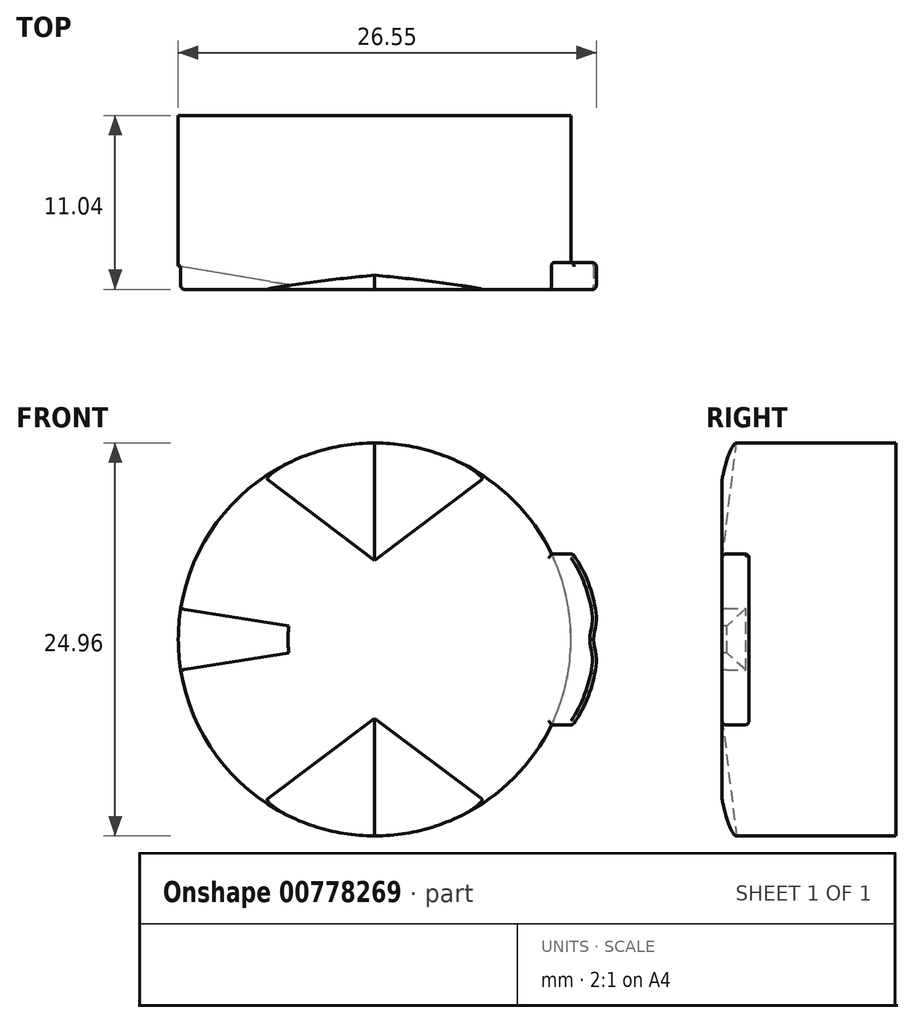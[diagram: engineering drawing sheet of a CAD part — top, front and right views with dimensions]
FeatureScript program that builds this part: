
annotation { "Feature Type Name" : "Feature", "Feature Type Description" : "" }
export const myFeature = defineFeature(function(context is Context, id is Id, definition is map)
    precondition{}
    {
        {
            var Q0;
            Q0=qCreatedBy(makeId("Front.planeOp"),FACE);
            var sketch = newSketch(context, id + "F0", { "sketchPlane" : qUnion([Q0])});
            skCircle(sketch, "E0", {"center": v(0, 0) * mm, "radius": 12.47 * mm});
            skSolve(sketch);
        }
        {
            var Q0;
            Q0=makeQuery(id+"F0.imprint","IMPRINT",FACE,{"disambiguationData":[TD([[makeQuery(id+"F0.imprint","IMPRINT",EDGE,{"derivedFrom":sQuery(id+"F0.wireOp",EDGE,"E0")}),1.0]])]});
            extrude(context, id + "F1", {"entities" : qUnion([Q0]), "depth" : 3.04 * mm, "offsetDistance" : 25 * mm});
        }
        {
            var Q0;
            Q0=makeQuery(id+"F1.opExtrude","CAP_FACE",FACE,{"disambiguationData":[OSD([sQuery(id+"F0.wireOp",EDGE,"E0")])],"isStart":false});
            var sketch = newSketch(context, id + "F2", { "sketchPlane" : qUnion([Q0])});
            skLineSegment(sketch, "E1", {"start": v(0, 0) * mm, "end": v(-7.03, 10.3) * mm, "construction": true});
            skLineSegment(sketch, "E2", {"start": v(0, 0) * mm, "end": v(0, 12.47) * mm, "construction": true});
            skLineSegment(sketch, "E3.MirrorCS", {"start": v(0, 0) * mm, "end": v(7.03, 10.3) * mm, "construction": true});
            skLineSegment(sketch, "E4", {"start": v(0, 0) * mm, "end": v(12.47, 0) * mm, "construction": true});
            skLineSegment(sketch, "E5.MirrorCS", {"start": v(0, 0) * mm, "end": v(7.03, -10.3) * mm, "construction": true});
            skLineSegment(sketch, "E6.MirrorCS", {"start": v(0, 0) * mm, "end": v(-7.03, -10.3) * mm, "construction": true});
            skLineSegment(sketch, "E7", {"start": v(11.42, -5.02) * mm, "end": v(-11.42, -5.02) * mm, "construction": true});
            skLineSegment(sketch, "E8", {"start": v(0, -5.02) * mm, "end": v(0, -12.47) * mm, "construction": true});
            skLineSegment(sketch, "E9", {"start": v(-7.03, -10.3) * mm, "end": v(0, -5.02) * mm});
            skLineSegment(sketch, "E10", {"start": v(7.03, -10.3) * mm, "end": v(0, -5.02) * mm, "construction": true});
            skLineSegment(sketch, "E11.MirrorCS", {"start": v(7.03, 10.3) * mm, "end": v(0, 5.02) * mm, "construction": true});
            skLineSegment(sketch, "E12.MirrorCS", {"start": v(-7.03, 10.3) * mm, "end": v(0, 5.02) * mm, "construction": true});
            skLineSegment(sketch, "E13", {"start": v(0, -5.02) * mm, "end": v(0, -12.47) * mm});
            skArc(sketch, "E14", {"start": v(0, -12.47) * mm, "mid": v(-3.68, -11.92) * mm, "end": v(-7.03, -10.3) * mm});
            skSolve(sketch);
        }
        {
            var Q0;
            Q0=qCreatedBy(makeId("Right.planeOp"),FACE);
            var sketch = newSketch(context, id + "F3", { "sketchPlane" : qUnion([Q0])});
            skLineSegment(sketch, "E15.0", {"start": v(-3.04, -5.02) * mm, "end": v(-3.04, -12.47) * mm});
            skLineSegment(sketch, "E16", {"start": v(-3.04, -12.47) * mm, "end": v(-2.14, -12.47) * mm});
            skLineSegment(sketch, "E17", {"start": v(-2.14, -12.47) * mm, "end": v(-3.04, -5.02) * mm});
            skLineSegment(sketch, "E18", {"start": v(-3.04, -5.02) * mm, "end": v(-7.03, -5.02) * mm, "construction": true});
            skPoint(sketch, "E19.0", {"position": v(-3.04, 0) * mm});
            skLineSegment(sketch, "E20", {"start": v(-3.04, 0) * mm, "end": v(-13.95, 0) * mm});
            skLineSegment(sketch, "E21.MirrorCS", {"start": v(-3.04, 12.47) * mm, "end": v(-2.14, 12.47) * mm});
            skLineSegment(sketch, "E22.0", {"start": v(-3.04, 0) * mm, "end": v(-3.04, 12.47) * mm});
            skPoint(sketch, "E23.0", {"position": v(-3.04, 7.66) * mm});
            skLineSegment(sketch, "E24.0", {"start": v(-3.04, 10.3) * mm, "end": v(-3.04, 5.02) * mm});
            skLineSegment(sketch, "E25", {"start": v(-3.04, 5.02) * mm, "end": v(-2.14, 12.47) * mm});
            skLineSegment(sketch, "E26", {"start": v(-3.04, 10.3) * mm, "end": v(-2.4, 10.3) * mm});
            skSolve(sketch);
        }
        {
            var Q0;
            Q0=sQuery(id+"F2.wireOp",EDGE,"E7");
            cPoint(context, id + "F4", {"entities" : qUnion([Q0]), "parameter" : 0.5});
        }
        {
            var Q0;
            Q0=qCreatedBy(id+"F4",VERTEX);
            var Q1;
            Q1=sQuery(id+"F2.wireOp",VERTEX,"E6.MirrorCS.end");
            var Q2;
            Q2=sQuery(id+"F3.wireOp",VERTEX,"E16.end");
            cPlane(context, id + "F5", {"entities" : qUnion([Q0, Q1, Q2]), "cplaneType" : CPlaneType.THREE_POINT, "offset" : 25 * mm, "width" : 150 * mm, "height" : 150 * mm});
        }
        {
            var Q0;
            Q0=qSketchRegion(id+"F2",true);
            var Q1;
            Q1=qCreatedBy(id+"F5.planeOp",FACE);
            extrude(context, id + "F6", {"entities" : qUnion([Q0]), "operationType" : NewBodyOperationType.REMOVE, "endBound" : BoundingType.UP_TO_SURFACE, "oppositeDirection" : true, "depth" : 25 * mm, "endBoundEntityFace" : qUnion([Q1]), "offsetDistance" : 25 * mm});
        }
        {
            var Q0;
            Q0=sQuery(id+"F2.wireOp",VERTEX,"E8.start");
            var Q1;
            Q1=makeQuery(id+"F6.boolean.opBoolean","COPY",VERTEX,{"derivedFrom":makeQuery(id+"F6.opExtrude","CAP_VERTEX",VERTEX,{"disambiguationData":[OSD([sQuery(id+"F2.wireOp",EDGE,"E13"),sQuery(id+"F2.wireOp",EDGE,"E14")])],"isStart":false})});
            var Q2;
            Q2=sQuery(id+"F2.wireOp",VERTEX,"E5.MirrorCS.end");
            cPlane(context, id + "F7", {"entities" : qUnion([Q0, Q1, Q2]), "cplaneType" : CPlaneType.THREE_POINT, "offset" : 25 * mm, "width" : 150 * mm, "height" : 150 * mm});
        }
        {
            var Q0;
            {var subQ0=sQuery(id+"F2.wireOp",EDGE,"E9");Q0=makeQuery(id+"F2.imprint","IMPRINT",FACE,{"disambiguationData":[TD([[makeQuery(id+"F2.imprint","IMPRINT",EDGE,{"derivedFrom":subQ0}),1.0]])]});}
            var sketch = newSketch(context, id + "F8", { "sketchPlane" : qUnion([Q0])});
            skLineSegment(sketch, "E27.0", {"start": v(7.03, -10.3) * mm, "end": v(0, -5.02) * mm});
            skLineSegment(sketch, "E28.0", {"start": v(0, -5.02) * mm, "end": v(0, -12.47) * mm});
            skArc(sketch, "E29", {"start": v(7.03, -10.3) * mm, "mid": v(3.68, -11.92) * mm, "end": v(0, -12.48) * mm});
            skSolve(sketch);
        }
        {
            var Q0;
            Q0=qSketchRegion(id+"F8",true);
            var Q1;
            Q1=qCreatedBy(id+"F7.planeOp",FACE);
            extrude(context, id + "F9", {"entities" : qUnion([Q0]), "operationType" : NewBodyOperationType.REMOVE, "endBound" : BoundingType.UP_TO_SURFACE, "oppositeDirection" : true, "depth" : 25 * mm, "endBoundEntityFace" : qUnion([Q1]), "offsetDistance" : 25 * mm});
        }
        {
            var Q0;
            Q0=sQuery(id+"F3.wireOp",VERTEX,"E26.end");
            var Q1;
            Q1=sQuery(id+"F2.wireOp",VERTEX,"E1.end");
            var Q2;
            Q2=sQuery(id+"F2.wireOp",VERTEX,"E3.MirrorCS.end");
            cPlane(context, id + "F10", {"entities" : qUnion([Q0, Q1, Q2]), "cplaneType" : CPlaneType.THREE_POINT, "offset" : 25 * mm, "width" : 150 * mm, "height" : 150 * mm});
        }
        {
            var Q0;
            Q0=qCreatedBy(id+"F10.planeOp",FACE);
            var sketch = newSketch(context, id + "F11", { "sketchPlane" : qUnion([Q0])});
            skPoint(sketch, "E30.0", {"position": v(7.03, 3.04) * mm});
            skPoint(sketch, "E31.0", {"position": v(0, 2.4) * mm});
            skPoint(sketch, "E32.0", {"position": v(-7.03, 3.04) * mm});
            skLineSegment(sketch, "E33", {"start": v(0, 2.4) * mm, "end": v(7.03, 3.04) * mm});
            skLineSegment(sketch, "E34", {"start": v(-7.03, 3.04) * mm, "end": v(0, 2.4) * mm});
            skLineSegment(sketch, "E35", {"start": v(-7.03, 3.04) * mm, "end": v(7.03, 3.04) * mm});
            skSolve(sketch);
        }
        {
            var Q0;
            Q0=qCreatedBy(makeId("Right.planeOp"),FACE);
            var sketch = newSketch(context, id + "F12", { "sketchPlane" : qUnion([Q0])});
            skPoint(sketch, "E36.0", {"position": v(-2.4, 10.3) * mm});
            skPoint(sketch, "E37.0", {"position": v(-3.04, 5.02) * mm});
            skLineSegment(sketch, "E38", {"start": v(-3.04, 5.02) * mm, "end": v(-2.4, 10.3) * mm});
            skPoint(sketch, "E39.0", {"position": v(-2.14, 12.47) * mm});
            skLineSegment(sketch, "E40", {"start": v(-2.4, 10.3) * mm, "end": v(-2.14, 12.47) * mm});
            skSolve(sketch);
        }
        {
            var Q0;
            Q0=sQuery(id+"F12.wireOp",VERTEX,"E39.0");
            var Q1;
            Q1=sQuery(id+"F12.wireOp",VERTEX,"E37.0");
            var Q2;
            Q2=sQuery(id+"F11.wireOp",VERTEX,"E32.0");
            cPlane(context, id + "F13", {"entities" : qUnion([Q0, Q1, Q2]), "cplaneType" : CPlaneType.THREE_POINT, "offset" : 25 * mm, "width" : 150 * mm, "height" : 150 * mm});
        }
        {
            var Q0;
            Q0=sQuery(id+"F12.wireOp",VERTEX,"E39.0");
            var Q1;
            Q1=sQuery(id+"F12.wireOp",VERTEX,"E37.0");
            var Q2;
            Q2=sQuery(id+"F11.wireOp",VERTEX,"E30.0");
            cPlane(context, id + "F14", {"entities" : qUnion([Q0, Q1, Q2]), "cplaneType" : CPlaneType.THREE_POINT, "offset" : 25 * mm, "width" : 150 * mm, "height" : 150 * mm});
        }
        {
            var Q0;
            {var subQ0=sQuery(id+"F2.wireOp",EDGE,"E9");Q0=makeQuery(id+"F2.imprint","IMPRINT",FACE,{"disambiguationData":[TD([[makeQuery(id+"F2.imprint","IMPRINT",EDGE,{"derivedFrom":subQ0}),1.0]])]});}
            var sketch = newSketch(context, id + "F15", { "sketchPlane" : qUnion([Q0])});
            skLineSegment(sketch, "E41.0", {"start": v(7.03, 10.3) * mm, "end": v(0, 5.02) * mm});
            skPoint(sketch, "E42.0", {"position": v(0, 12.47) * mm});
            skLineSegment(sketch, "E43", {"start": v(0, 5.02) * mm, "end": v(0, 12.47) * mm});
            skArc(sketch, "E44", {"start": v(7.03, 10.3) * mm, "mid": v(3.68, 11.92) * mm, "end": v(0, 12.48) * mm});
            skSolve(sketch);
        }
        {
            var Q0;
            Q0=qSketchRegion(id+"F15",true);
            var Q1;
            Q1=qCreatedBy(id+"F14.planeOp",FACE);
            extrude(context, id + "F16", {"entities" : qUnion([Q0]), "operationType" : NewBodyOperationType.REMOVE, "endBound" : BoundingType.UP_TO_SURFACE, "oppositeDirection" : true, "depth" : 25 * mm, "endBoundEntityFace" : qUnion([Q1]), "offsetDistance" : 25 * mm});
        }
        {
            var Q0;
            {var subQ0=sQuery(id+"F2.wireOp",EDGE,"E9");Q0=makeQuery(id+"F2.imprint","IMPRINT",FACE,{"disambiguationData":[TD([[makeQuery(id+"F2.imprint","IMPRINT",EDGE,{"derivedFrom":subQ0}),1.0]])]});}
            var sketch = newSketch(context, id + "F17", { "sketchPlane" : qUnion([Q0])});
            skLineSegment(sketch, "E45.0", {"start": v(-7.03, 10.3) * mm, "end": v(0, 5.02) * mm});
            skPoint(sketch, "E46.0", {"position": v(0, 12.47) * mm});
            skLineSegment(sketch, "E47", {"start": v(0, 5.02) * mm, "end": v(0, 12.47) * mm});
            skArc(sketch, "E48", {"start": v(0, 12.47) * mm, "mid": v(-3.68, 11.92) * mm, "end": v(-7.03, 10.3) * mm});
            skSolve(sketch);
        }
        {
            var Q0;
            Q0=qSketchRegion(id+"F17",true);
            var Q1;
            Q1=qCreatedBy(id+"F13.planeOp",FACE);
            extrude(context, id + "F18", {"entities" : qUnion([Q0]), "operationType" : NewBodyOperationType.REMOVE, "endBound" : BoundingType.UP_TO_SURFACE, "oppositeDirection" : true, "depth" : 25 * mm, "endBoundEntityFace" : qUnion([Q1]), "offsetDistance" : 25 * mm});
        }
        {
            var Q0;
            Q0=makeQuery(id+"F1.opExtrude","CAP_FACE",FACE,{"disambiguationData":[OSD([sQuery(id+"F0.wireOp",EDGE,"E0")])],"isStart":false});
            var sketch = newSketch(context, id + "F19", { "sketchPlane" : qUnion([Q0])});
            skLineSegment(sketch, "E49", {"start": v(0, 0) * mm, "end": v(33.2, 0) * mm, "construction": true});
            skLineSegment(sketch, "E50", {"start": v(17.66, 5.43) * mm, "end": v(11.23, 5.43) * mm, "construction": true});
            skLineSegment(sketch, "E51", {"start": v(11.23, 5.43) * mm, "end": v(12.58, 5.43) * mm});
            skFitSpline(sketch, "E52", {"points": [v(12.58, 5.43) * mm, v(14.07, 1.3) * mm, v(13.9, 0) * mm], "startDerivative": vector(4.4, -5.8) * mm, "endDerivative": vector(0, -4.14) * mm});
            skFitSpline(sketch, "E53.MirrorCS", {"points": [v(12.58, -5.43) * mm, v(14.07, -1.3) * mm, v(13.9, 0) * mm], "startDerivative": vector(4.4, 5.8) * mm, "endDerivative": vector(0, 4.14) * mm});
            skLineSegment(sketch, "E54.MirrorCS", {"start": v(17.66, -5.43) * mm, "end": v(11.23, -5.43) * mm, "construction": true});
            skLineSegment(sketch, "E55", {"start": v(12.58, -5.43) * mm, "end": v(11.23, -5.43) * mm});
            skArc(sketch, "E56", {"start": v(11.23, 5.43) * mm, "mid": v(12.47, 0) * mm, "end": v(11.23, -5.43) * mm});
            skSolve(sketch);
        }
        {
            var Q0;
            Q0=makeQuery(id+"F19.imprint","IMPRINT",FACE,{"disambiguationData":[TD([[makeQuery(id+"F19.imprint","IMPRINT",EDGE,{"derivedFrom":sQuery(id+"F19.wireOp",EDGE,"E51")}),-1.0]])]});
            extrude(context, id + "F20", {"entities" : qUnion([Q0]), "operationType" : NewBodyOperationType.ADD, "oppositeDirection" : true, "depth" : 1.7 * mm, "offsetDistance" : 25 * mm});
        }
        {
            var Q0;
            {var subQ0=sQuery(id+"F19.wireOp",EDGE,"E56");var subQ1=sQuery(id+"F19.wireOp",EDGE,"E55");var subQ2=sQuery(id+"F19.wireOp",EDGE,"E53.MirrorCS");var subQ3=sQuery(id+"F19.wireOp",EDGE,"E52");var subQ4=sQuery(id+"F19.wireOp",EDGE,"E51");Q0=makeQuery(id+"FGMiUAum6pMF5fA_1.1.F20.boolean.opBoolean","MERGE",FACE,{"derivedFrom":[makeQuery(id+"F20.boolean.opBoolean","MERGE",FACE,{"derivedFrom":[makeQuery(id+"F1.opExtrude","CAP_FACE",FACE,{"disambiguationData":[OSD([sQuery(id+"F0.wireOp",EDGE,"E0")])],"isStart":false}),makeQuery(id+"F20.opExtrude","CAP_FACE",FACE,{"disambiguationData":[OSD([subQ4,subQ3,subQ2,subQ1,subQ0])],"isStart":true})]}),makeQuery(id+"FGMiUAum6pMF5fA_1.1.F20.opExtrude","CAP_FACE",FACE,{"disambiguationData":[OSD([subQ4,subQ3,subQ2,subQ1,subQ0])],"isStart":true})]});}
            var sketch = newSketch(context, id + "F21", { "sketchPlane" : qUnion([Q0])});
            skCircle(sketch, "E57", {"center": v(0, 0) * mm, "radius": 12.47 * mm, "construction": true});
            skLineSegment(sketch, "E58", {"start": v(12.47, 0) * mm, "end": v(-12.47, 0) * mm, "construction": true});
            skLineSegment(sketch, "E59", {"start": v(12.31, 0) * mm, "end": v(12.31, 2) * mm, "construction": true});
            skLineSegment(sketch, "E60", {"start": v(5.51, 0) * mm, "end": v(5.51, 0.7) * mm, "construction": true});
            skLineSegment(sketch, "E61", {"start": v(5.51, 0) * mm, "end": v(5.51, 0.7) * mm});
            skLineSegment(sketch, "E62", {"start": v(12.31, 2) * mm, "end": v(5.51, 0.7) * mm});
            skLineSegment(sketch, "E63.MirrorCS", {"start": v(12.31, -2) * mm, "end": v(5.51, -0.7) * mm});
            skLineSegment(sketch, "E64.MirrorCS", {"start": v(5.51, 0) * mm, "end": v(5.51, -0.7) * mm, "construction": true});
            skArc(sketch, "E65", {"start": v(12.31, 2) * mm, "mid": v(12.47, 0) * mm, "end": v(12.31, -2) * mm});
            skLineSegment(sketch, "E66", {"start": v(0, 0) * mm, "end": v(0, 4.2) * mm, "construction": true});
            skLineSegment(sketch, "E67.MirrorCS", {"start": v(-12.31, 2) * mm, "end": v(-5.51, 0.7) * mm});
            skLineSegment(sketch, "E68.MirrorCS", {"start": v(-5.51, 0) * mm, "end": v(-5.51, 0.7) * mm, "construction": true});
            skLineSegment(sketch, "E69.MirrorCS", {"start": v(-5.51, 0) * mm, "end": v(-5.51, -0.7) * mm, "construction": true});
            skLineSegment(sketch, "E70.MirrorCS", {"start": v(-12.31, -2) * mm, "end": v(-5.51, -0.7) * mm});
            skArc(sketch, "E71.MirrorCS", {"start": v(-12.31, 2) * mm, "mid": v(-12.47, 0) * mm, "end": v(-12.31, -2) * mm});
            skSolve(sketch);
        }
        {
            var Q0;
            Q0=qCreatedBy(makeId("Top.planeOp"),FACE);
            var sketch = newSketch(context, id + "F22", { "sketchPlane" : qUnion([Q0])});
            skPoint(sketch, "E72.0", {"position": v(5.51, -3.04) * mm});
            skPoint(sketch, "E73.0", {"position": v(12.47, -3.04) * mm});
            skPoint(sketch, "E74.0", {"position": v(-5.51, -3.04) * mm});
            skPoint(sketch, "E75.0", {"position": v(-12.47, -3.04) * mm});
            skPoint(sketch, "E76.0", {"position": v(0, -3.04) * mm});
            skLineSegment(sketch, "E77", {"start": v(0, -3.04) * mm, "end": v(0, -11.42) * mm, "construction": true});
            skLineSegment(sketch, "E78", {"start": v(-12.47, -3.04) * mm, "end": v(-12.47, -1.54) * mm});
            skLineSegment(sketch, "E79", {"start": v(-12.47, -1.54) * mm, "end": v(-5.51, -2.74) * mm});
            skLineSegment(sketch, "E80", {"start": v(-5.51, -2.74) * mm, "end": v(-5.51, -3.04) * mm});
            skLineSegment(sketch, "E81", {"start": v(-12.47, -3.04) * mm, "end": v(-5.51, -3.04) * mm});
            skSolve(sketch);
        }
        {
            var Q0;
            Q0=qSketchRegion(id+"F22",true);
            var Q1;
            Q1=sQuery(id+"F22.wireOp",EDGE,"E77");
            revolve(context, id + "F23", {"operationType" : NewBodyOperationType.REMOVE, "surfaceOperationType" : NewSurfaceOperationType.NEW, "entities" : qUnion([Q0]), "axis" : qUnion([Q1]), "revolveType" : RevolveType.SYMMETRIC, "angle" : 18 * degree});
        }
        {
            var Q0;
            Q0=makeQuery(id+"F6.boolean.opBoolean","COPY",EDGE,{"derivedFrom":makeQuery(id+"F6.opExtrude","CAP_EDGE",EDGE,{"disambiguationData":[OSD([sQuery(id+"F2.wireOp",EDGE,"E14")])],"isStart":false})});
            var Q1;
            {var subQ1=sQuery(id+"F19.wireOp",EDGE,"E55");var subQ6=sQuery(id+"F0.wireOp",EDGE,"E0");Q1=makeQuery(id+"FGMiUAum6pMF5fA_1.1.F20.boolean.opBoolean","SPLIT",EDGE,{"disambiguationData":[TD([makeQuery(id+"FGMiUAum6pMF5fA_1.1.F20.opExtrude","SWEPT_FACE",FACE,{"disambiguationData":[OSD([subQ1])]})])],"derivedFrom":makeQuery(id+"F16.boolean.opBoolean","SPLIT",EDGE,{"disambiguationData":[TD([makeQuery(id+"F16.opExtrude","SWEPT_FACE",FACE,{"disambiguationData":[OSD([sQuery(id+"F15.wireOp",EDGE,"E43")])]})])],"derivedFrom":makeQuery(id+"F1.opExtrude","CAP_EDGE",EDGE,{"disambiguationData":[OSD([subQ6])],"isStart":false})})});}
            var Q2;
            Q2=makeQuery(id+"FGMiUAum6pMF5fA_1.1.F20.opExtrude","CAP_EDGE",EDGE,{"disambiguationData":[OSD([sQuery(id+"F19.wireOp",EDGE,"E55")])],"isStart":true});
            var Q3;
            Q3=makeQuery(id+"FGMiUAum6pMF5fA_1.1.F20.opExtrude","CAP_EDGE",EDGE,{"disambiguationData":[OSD([sQuery(id+"F19.wireOp",EDGE,"E53.MirrorCS")])],"isStart":true});
            var Q4;
            Q4=makeQuery(id+"FGMiUAum6pMF5fA_1.1.F20.opExtrude","CAP_EDGE",EDGE,{"disambiguationData":[OSD([sQuery(id+"F19.wireOp",EDGE,"E51")])],"isStart":true});
            var Q5;
            {var subQ4=sQuery(id+"F19.wireOp",EDGE,"E51");var subQ5=sQuery(id+"F0.wireOp",EDGE,"E0");Q5=makeQuery(id+"FGMiUAum6pMF5fA_1.1.F20.boolean.opBoolean","SPLIT",EDGE,{"disambiguationData":[TD([makeQuery(id+"FGMiUAum6pMF5fA_1.1.F20.opExtrude","SWEPT_FACE",FACE,{"disambiguationData":[OSD([subQ4])]})])],"derivedFrom":makeQuery(id+"F16.boolean.opBoolean","SPLIT",EDGE,{"disambiguationData":[TD([makeQuery(id+"F16.opExtrude","SWEPT_FACE",FACE,{"disambiguationData":[OSD([sQuery(id+"F15.wireOp",EDGE,"E43")])]})])],"derivedFrom":makeQuery(id+"F1.opExtrude","CAP_EDGE",EDGE,{"disambiguationData":[OSD([subQ5])],"isStart":false})})});}
            var Q6;
            Q6=makeQuery(id+"F18.boolean.opBoolean","COPY",EDGE,{"derivedFrom":makeQuery(id+"F18.opExtrude","TWEAK_EDGE",EDGE,{"derivedFrom":[dummyQuery(id+"F13.planeOp",FACE),makeQuery(id+"F17.imprint","IMPRINT",EDGE,{"derivedFrom":sQuery(id+"F17.wireOp",EDGE,"E48")})]})});
            var Q7;
            Q7=makeQuery(id+"F16.boolean.opBoolean","COPY",EDGE,{"derivedFrom":makeQuery(id+"F16.opExtrude","CAP_EDGE",EDGE,{"disambiguationData":[OSD([sQuery(id+"F15.wireOp",EDGE,"E44")])],"isStart":false})});
            var Q8;
            {var subQ1=sQuery(id+"F19.wireOp",EDGE,"E51");var subQ2=sQuery(id+"F0.wireOp",EDGE,"E0");Q8=makeQuery(id+"F20.boolean.opBoolean","SPLIT",EDGE,{"disambiguationData":[TD([makeQuery(id+"F20.opExtrude","SWEPT_FACE",FACE,{"disambiguationData":[OSD([subQ1])]})])],"derivedFrom":makeQuery(id+"F16.boolean.opBoolean","SPLIT",EDGE,{"disambiguationData":[TD([makeQuery(id+"F9.boolean.opBoolean","COPY",FACE,{"derivedFrom":makeQuery(id+"F9.opExtrude","CAP_FACE",FACE,{"disambiguationData":[OSD([sQuery(id+"F8.wireOp",EDGE,"E27.0"),sQuery(id+"F8.wireOp",EDGE,"E28.0"),sQuery(id+"F8.wireOp",EDGE,"E29")])],"isStart":false})})])],"derivedFrom":makeQuery(id+"F1.opExtrude","CAP_EDGE",EDGE,{"disambiguationData":[OSD([subQ2])],"isStart":false})})});}
            var Q9;
            Q9=makeQuery(id+"F20.opExtrude","CAP_EDGE",EDGE,{"disambiguationData":[OSD([sQuery(id+"F19.wireOp",EDGE,"E51")])],"isStart":true});
            var Q10;
            Q10=makeQuery(id+"F20.opExtrude","CAP_EDGE",EDGE,{"disambiguationData":[OSD([sQuery(id+"F19.wireOp",EDGE,"E52")])],"isStart":true});
            var Q11;
            Q11=makeQuery(id+"F20.opExtrude","CAP_EDGE",EDGE,{"disambiguationData":[OSD([sQuery(id+"F19.wireOp",EDGE,"E55")])],"isStart":true});
            var Q12;
            {var subQ0=sQuery(id+"F19.wireOp",EDGE,"E55");var subQ1=makeQuery(id+"F9.boolean.opBoolean","COPY",FACE,{"derivedFrom":makeQuery(id+"F9.opExtrude","CAP_FACE",FACE,{"disambiguationData":[OSD([sQuery(id+"F8.wireOp",EDGE,"E27.0"),sQuery(id+"F8.wireOp",EDGE,"E28.0"),sQuery(id+"F8.wireOp",EDGE,"E29")])],"isStart":false})});var subQ2=sQuery(id+"F0.wireOp",EDGE,"E0");Q12=makeQuery(id+"F20.boolean.opBoolean","SPLIT",EDGE,{"disambiguationData":[TD([makeQuery(id+"F20.opExtrude","SWEPT_FACE",FACE,{"disambiguationData":[OSD([subQ0])]})])],"derivedFrom":makeQuery(id+"F16.boolean.opBoolean","SPLIT",EDGE,{"disambiguationData":[TD([subQ1])],"derivedFrom":makeQuery(id+"F1.opExtrude","CAP_EDGE",EDGE,{"disambiguationData":[OSD([subQ2])],"isStart":false})})});}
            var Q13;
            Q13=makeQuery(id+"F9.boolean.opBoolean","COPY",EDGE,{"derivedFrom":makeQuery(id+"F9.opExtrude","TWEAK_EDGE",EDGE,{"derivedFrom":[dummyQuery(id+"F7.planeOp",FACE),makeQuery(id+"F8.imprint","IMPRINT",EDGE,{"derivedFrom":sQuery(id+"F8.wireOp",EDGE,"E29")})]})});
            var Q14;
            Q14=makeQuery(id+"FGMiUAum6pMF5fA_1.1.F20.opExtrude","SWEPT_EDGE",EDGE,{"disambiguationData":[OSD([sQuery(id+"F19.wireOp",EDGE,"E53.MirrorCS"),sQuery(id+"F19.wireOp",EDGE,"E55")])]});
            var Q15;
            Q15=makeQuery(id+"FGMiUAum6pMF5fA_1.1.F20.opExtrude","CAP_EDGE",EDGE,{"disambiguationData":[OSD([sQuery(id+"F19.wireOp",EDGE,"E55")])],"isStart":false});
            var Q16;
            Q16=makeQuery(id+"FGMiUAum6pMF5fA_1.1.F20.opExtrude","CAP_EDGE",EDGE,{"disambiguationData":[OSD([sQuery(id+"F19.wireOp",EDGE,"E53.MirrorCS")])],"isStart":false});
            var Q17;
            Q17=makeQuery(id+"FGMiUAum6pMF5fA_1.1.F20.opExtrude","SWEPT_EDGE",EDGE,{"disambiguationData":[OSD([sQuery(id+"F19.wireOp",EDGE,"E51"),sQuery(id+"F19.wireOp",EDGE,"E52")])]});
            var Q18;
            Q18=makeQuery(id+"FGMiUAum6pMF5fA_1.1.F20.opExtrude","CAP_EDGE",EDGE,{"disambiguationData":[OSD([sQuery(id+"F19.wireOp",EDGE,"E51")])],"isStart":false});
            var Q19;
            Q19=makeQuery(id+"F20.opExtrude","SWEPT_EDGE",EDGE,{"disambiguationData":[OSD([sQuery(id+"F19.wireOp",EDGE,"E51"),sQuery(id+"F19.wireOp",EDGE,"E52")])]});
            var Q20;
            Q20=makeQuery(id+"F20.opExtrude","CAP_EDGE",EDGE,{"disambiguationData":[OSD([sQuery(id+"F19.wireOp",EDGE,"E51")])],"isStart":false});
            var Q21;
            Q21=makeQuery(id+"F20.opExtrude","CAP_EDGE",EDGE,{"disambiguationData":[OSD([sQuery(id+"F19.wireOp",EDGE,"E52")])],"isStart":false});
            var Q22;
            Q22=makeQuery(id+"F20.opExtrude","CAP_EDGE",EDGE,{"disambiguationData":[OSD([sQuery(id+"F19.wireOp",EDGE,"E55")])],"isStart":false});
            var Q23;
            Q23=makeQuery(id+"F20.opExtrude","SWEPT_EDGE",EDGE,{"disambiguationData":[OSD([sQuery(id+"F19.wireOp",EDGE,"E53.MirrorCS"),sQuery(id+"F19.wireOp",EDGE,"E55")])]});
            fillet(context, id + "F24", {"entities" : qUnion([Q0, Q1, Q2, Q3, Q4, Q5, Q6, Q7, Q8, Q9, Q10, Q11, Q12, Q13, Q14, Q15, Q16, Q17, Q18, Q19, Q20, Q21, Q22, Q23]), "radius" : .25 * mm, "tangentPropagation" : true, "allowEdgeOverflow" : false});
        }
        {
            var Q0;
            Q0=makeQuery(id+"F1.opExtrude","CAP_FACE",FACE,{"disambiguationData":[OSD([sQuery(id+"F0.wireOp",EDGE,"E0")])],"isStart":true});
            var sketch = newSketch(context, id + "F25", { "sketchPlane" : qUnion([Q0])});
            skCircle(sketch, "E82.0", {"center": v(0, 0) * mm, "radius": 12.47 * mm});
            skSolve(sketch);
        }
        {
            var Q0;
            Q0=makeQuery(id+"F25.imprint","IMPRINT",FACE,{"disambiguationData":[TD([[makeQuery(id+"F25.imprint","IMPRINT",EDGE,{"derivedFrom":sQuery(id+"F25.wireOp",EDGE,"E82.0")}),-1.0]])]});
            extrude(context, id + "F26", {"entities" : qUnion([Q0]), "operationType" : NewBodyOperationType.ADD, "depth" : 8 * mm, "offsetDistance" : 25 * mm});
        }
    });
